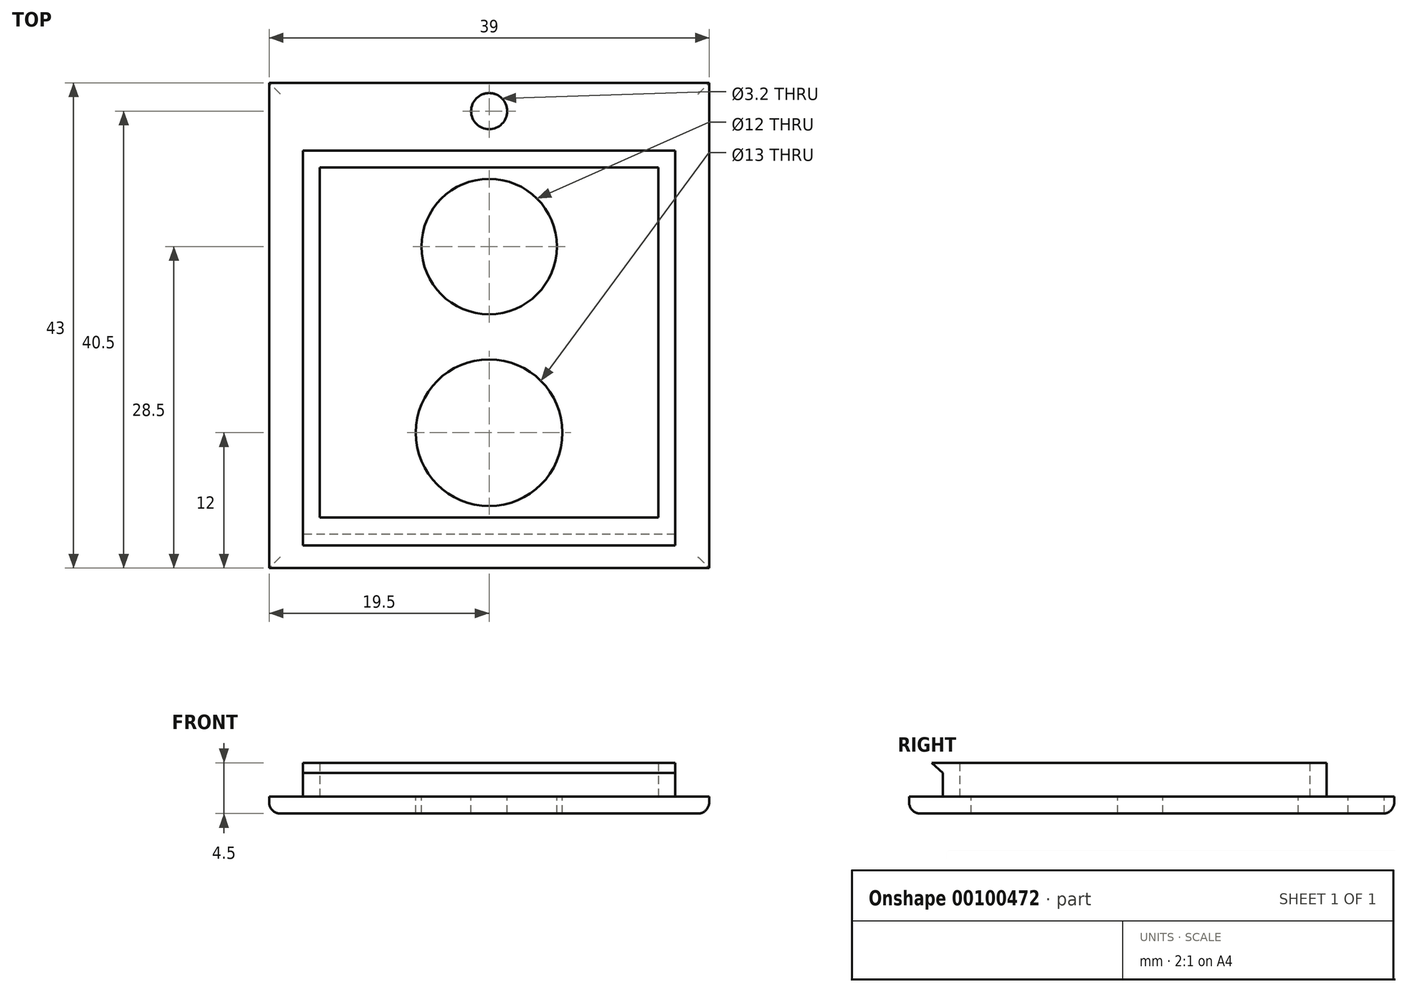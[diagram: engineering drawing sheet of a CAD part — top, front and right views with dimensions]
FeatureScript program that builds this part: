
annotation { "Feature Type Name" : "Feature", "Feature Type Description" : "" }
export const myFeature = defineFeature(function(context is Context, id is Id, definition is map)
    precondition{}
    {
        {
            var Q0;
            Q0=qCreatedBy(makeId("Top.planeOp"),FACE);
            var sketch = newSketch(context, id + "F0", { "sketchPlane" : qUnion([Q0])});
            skLineSegment(sketch, "E0.bottom", {"start": v(-16.5, 17) * mm, "end": v(16.5, 17) * mm});
            skLineSegment(sketch, "E0.top", {"start": v(-16.5, -17) * mm, "end": v(16.5, -17) * mm});
            skLineSegment(sketch, "E0.left", {"start": v(-16.5, 17) * mm, "end": v(-16.5, -17) * mm});
            skLineSegment(sketch, "E0.right", {"start": v(16.5, 17) * mm, "end": v(16.5, -17) * mm});
            skLineSegment(sketch, "E1.bottom", {"start": v(-15, 15.5) * mm, "end": v(15, 15.5) * mm});
            skLineSegment(sketch, "E1.top", {"start": v(-15, -15.5) * mm, "end": v(15, -15.5) * mm});
            skLineSegment(sketch, "E1.left", {"start": v(-15, 15.5) * mm, "end": v(-15, -15.5) * mm});
            skLineSegment(sketch, "E1.right", {"start": v(15, 15.5) * mm, "end": v(15, -15.5) * mm});
            skSolve(sketch);
        }
        {
            var Q0;
            Q0=makeQuery(id+"F0.imprint","IMPRINT",FACE,{"disambiguationData":[TD([[makeQuery(id+"F0.imprint","IMPRINT",EDGE,{"derivedFrom":sQuery(id+"F0.wireOp",EDGE,"E0.bottom")}),-1.0]])]});
            extrude(context, id + "F1", {"entities" : qUnion([Q0]), "depth" : 3 * mm});
        }
        {
            var Q0;
            Q0=qCreatedBy(makeId("Top.planeOp"),FACE);
            var sketch = newSketch(context, id + "F2", { "sketchPlane" : qUnion([Q0])});
            skLineSegment(sketch, "E2.bottom", {"start": v(-19.5, -20) * mm, "end": v(19.5, -20) * mm});
            skLineSegment(sketch, "E2.top", {"start": v(-19.5, 23) * mm, "end": v(19.5, 23) * mm});
            skLineSegment(sketch, "E2.left", {"start": v(-19.5, -20) * mm, "end": v(-19.5, 23) * mm});
            skLineSegment(sketch, "E2.right", {"start": v(19.5, -20) * mm, "end": v(19.5, 23) * mm});
            skPoint(sketch, "E3", {"position": v(0, 20.5) * mm});
            skPoint(sketch, "E4", {"position": v(0, 8.5) * mm});
            skPoint(sketch, "E5", {"position": v(0, -8) * mm});
            skSolve(sketch);
        }
        {
            var Q0;
            Q0=makeQuery(id+"F2.imprint","IMPRINT",FACE,{"disambiguationData":[TD([[makeQuery(id+"F2.imprint","IMPRINT",EDGE,{"derivedFrom":sQuery(id+"F2.wireOp",EDGE,"E2.bottom")}),1.0]])]});
            extrude(context, id + "F3", {"entities" : qUnion([Q0]), "operationType" : NewBodyOperationType.ADD, "oppositeDirection" : true, "depth" : 1.5 * mm});
        }
        {
            var Q0;
            Q0=sQuery(id+"F2.wireOp",VERTEX,"E3");
            var Q1;
            Q1=makeQuery(id+"F1.opExtrude","SWEPT_BODY",BODY,{"disambiguationData":[OSD([sQuery(id+"F0.wireOp",EDGE,"E0.bottom"),sQuery(id+"F0.wireOp",EDGE,"E0.top"),sQuery(id+"F0.wireOp",EDGE,"E0.left"),sQuery(id+"F0.wireOp",EDGE,"E0.right"),sQuery(id+"F0.wireOp",EDGE,"E1.bottom"),sQuery(id+"F0.wireOp",EDGE,"E1.top"),sQuery(id+"F0.wireOp",EDGE,"E1.left"),sQuery(id+"F0.wireOp",EDGE,"E1.right")])]});
            hole(context, id + "F4", {"style" : HoleStyle.SIMPLE, "endStyle" : HoleEndStyle.THROUGH, "holeDiameter" : 3.2 * mm, "locations" : qUnion([Q0]), "scope" : qUnion([Q1]), "isTappedThrough" : true});
        }
        {
            var Q0;
            Q0=makeQuery(id+"F3.opExtrude","CAP_EDGE",EDGE,{"disambiguationData":[OSD([sQuery(id+"F2.wireOp",EDGE,"E2.top")])],"isStart":false});
            var Q1;
            Q1=makeQuery(id+"F3.opExtrude","CAP_EDGE",EDGE,{"disambiguationData":[OSD([sQuery(id+"F2.wireOp",EDGE,"E2.left")])],"isStart":false});
            var Q2;
            Q2=makeQuery(id+"F3.opExtrude","CAP_EDGE",EDGE,{"disambiguationData":[OSD([sQuery(id+"F2.wireOp",EDGE,"E2.bottom")])],"isStart":false});
            var Q3;
            Q3=makeQuery(id+"F3.opExtrude","CAP_EDGE",EDGE,{"disambiguationData":[OSD([sQuery(id+"F2.wireOp",EDGE,"E2.right")])],"isStart":false});
            fillet(context, id + "F5", {"entities" : qUnion([Q0, Q1, Q2, Q3]), "radius" : 1 * mm, "tangentPropagation" : true, "allowEdgeOverflow" : false});
        }
        {
            var Q0;
            Q0=qCreatedBy(makeId("Right.planeOp"),FACE);
            var sketch = newSketch(context, id + "F6", { "sketchPlane" : qUnion([Q0])});
            skLineSegment(sketch, "E6.top", {"start": v(-18, 3) * mm, "end": v(-17, 3) * mm});
            skLineSegment(sketch, "E6.right", {"start": v(-17, 2.1) * mm, "end": v(-17, 3) * mm});
            skLineSegment(sketch, "E7", {"start": v(-18, 3) * mm, "end": v(-17, 2.1) * mm});
            skSolve(sketch);
        }
        {
            var Q0;
            Q0 = qSketchRegion(id + "F6", true);
            extrude(context, id + "F7", {"entities" : qUnion([Q0]), "operationType" : NewBodyOperationType.ADD, "endBound" : BoundingType.SYMMETRIC, "depth" : 33 * mm});
        }
        {
            var Q0;
            Q0=sQuery(id+"F2.wireOp",VERTEX,"E4");
            var Q1;
            Q1=makeQuery(id+"F1.opExtrude","SWEPT_BODY",BODY,{"disambiguationData":[OSD([sQuery(id+"F0.wireOp",EDGE,"E0.bottom"),sQuery(id+"F0.wireOp",EDGE,"E0.top"),sQuery(id+"F0.wireOp",EDGE,"E0.left"),sQuery(id+"F0.wireOp",EDGE,"E0.right"),sQuery(id+"F0.wireOp",EDGE,"E1.bottom"),sQuery(id+"F0.wireOp",EDGE,"E1.top"),sQuery(id+"F0.wireOp",EDGE,"E1.left"),sQuery(id+"F0.wireOp",EDGE,"E1.right")])]});
            hole(context, id + "F8", {"style" : HoleStyle.SIMPLE, "endStyle" : HoleEndStyle.THROUGH, "holeDiameter" : 12 * mm, "locations" : qUnion([Q0]), "scope" : qUnion([Q1]), "isTappedThrough" : true});
        }
        {
            var Q0;
            Q0=sQuery(id+"F2.wireOp",VERTEX,"E5");
            var Q1;
            Q1=makeQuery(id+"F1.opExtrude","SWEPT_BODY",BODY,{"disambiguationData":[OSD([sQuery(id+"F0.wireOp",EDGE,"E0.bottom"),sQuery(id+"F0.wireOp",EDGE,"E0.top"),sQuery(id+"F0.wireOp",EDGE,"E0.left"),sQuery(id+"F0.wireOp",EDGE,"E0.right"),sQuery(id+"F0.wireOp",EDGE,"E1.bottom"),sQuery(id+"F0.wireOp",EDGE,"E1.top"),sQuery(id+"F0.wireOp",EDGE,"E1.left"),sQuery(id+"F0.wireOp",EDGE,"E1.right")])]});
            hole(context, id + "F9", {"style" : HoleStyle.SIMPLE, "endStyle" : HoleEndStyle.THROUGH, "holeDiameter" : 13 * mm, "locations" : qUnion([Q0]), "scope" : qUnion([Q1]), "isTappedThrough" : true});
        }
    });
